# Revit family: Data_Rack-Middle_Atlantic-Wall-Pivoting-SR_Series
name_source: partatom
category: Data Devices
units: mm (PartAtom-declared; Revit-internal decimal feet)

## family parameters
Cut with Voids When Loaded = No
Host = Face
Maintain Annotation Orientation = No
Part Type = Normal
Room Calculation Point = No
Round Connector Dimension = Use Diameter
Shared = No

## types (9) — shared parameters
Date Modified = February 5, 2021
Default Elevation = 48 "
Equipment Abbreviation = SR
Family Version = 1.0
Manufacturer = Middle Atlantic
Material = Powdercoat - Middle Atlantic - Black
Model Disclaimer = Contact Middle Atlantic For More Information
Product Documentation Link = https://res.cloudinary.com
Product Page URL = https://www.legrandav.com
URL = https://www.legrandav.com
zero-valued in all types: z RU Offset Depth

## per-type parameters (varying)
| type | Description | Model | Weight | z RU Count | z Type Depth | z Type Height | z Type Width |
| 24" Wide, 24RU, 28" Deep, SR-24-28 | SR Series Pivoting Wall Cabinet, 24RU, 24 In. Wide, 28 In. Deep | SR-24-28 | 115.000 lb | 24 | 28 | 24 | 24 |
| 24" Wide, 24RU, 32" Deep, SR-24-32 | SR Series Pivoting Wall Cabinet, 24RU, 24 In. Wide, 32 In. Deep | SR-24-32 | 131.000 lb | 24 | 32 | 24 | 24 |
| 24" Wide, 40RU, 28" Deep, SR-40-28 | SR Series Pivoting Wall Cabinet, 40RU, 24 In. Wide, 28 In. Deep | SR-40-28 | 185.000 lb | 40 | 28 | 40 | 24 |
| 24" Wide, 46RU, 28" Deep, SR-46-28 | SR Series Pivoting Wall Cabinet, 46RU, 24 In. Wide, 28 In. Deep | SR-46-28 | 207.000 lb | 46 | 28 | 46 | 24 |
| 24" Wide, 40RU, 32" Deep, SR-40-32 | SR Series Pivoting Wall Cabinet, 40RU, 24 In. Wide, 32 In. Deep | SR-40-32 | 200.000 lb | 40 | 32 | 40 | 24 |
| 24" Wide, 40RU, 22" Deep, SR-40-22 | SR Series Pivoting Wall Cabinet, 40RU, 24 In. Wide, 22 In. Deep | SR-40-22 | 170.000 lb | 40 | 22 | 40 | 24 |
| 28" Wide, 24RU, 32" Deep, SR28-24-32 | SR Series Pivoting Wall Cabinet, 24RU, 28 In. Wide, 32 In. Deep | SR28-24-32 | 155.000 lb | 24 | 32 | 24 | 28 |
| 28" Wide, 40RU, 32" Deep, SR28-40-32 | SR Series Pivoting Wall Cabinet, 40RU, 28 In. Wide, 32 In. Deep | SR28-40-32 | 248.000 lb | 40 | 32 | 40 | 28 |
| 28" Wide, 46RU, 32" Deep, SR28-46-32 | SR Series Pivoting Wall Cabinet, 46RU, 28 In. Wide, 32 In. Deep | SR28-46-32 | 254.000 lb | 46 | 32 | 46 | 28 |

## geometry (parser evidence)
native form markers: Sweep x6
no freeform markers — native parametric forms only
